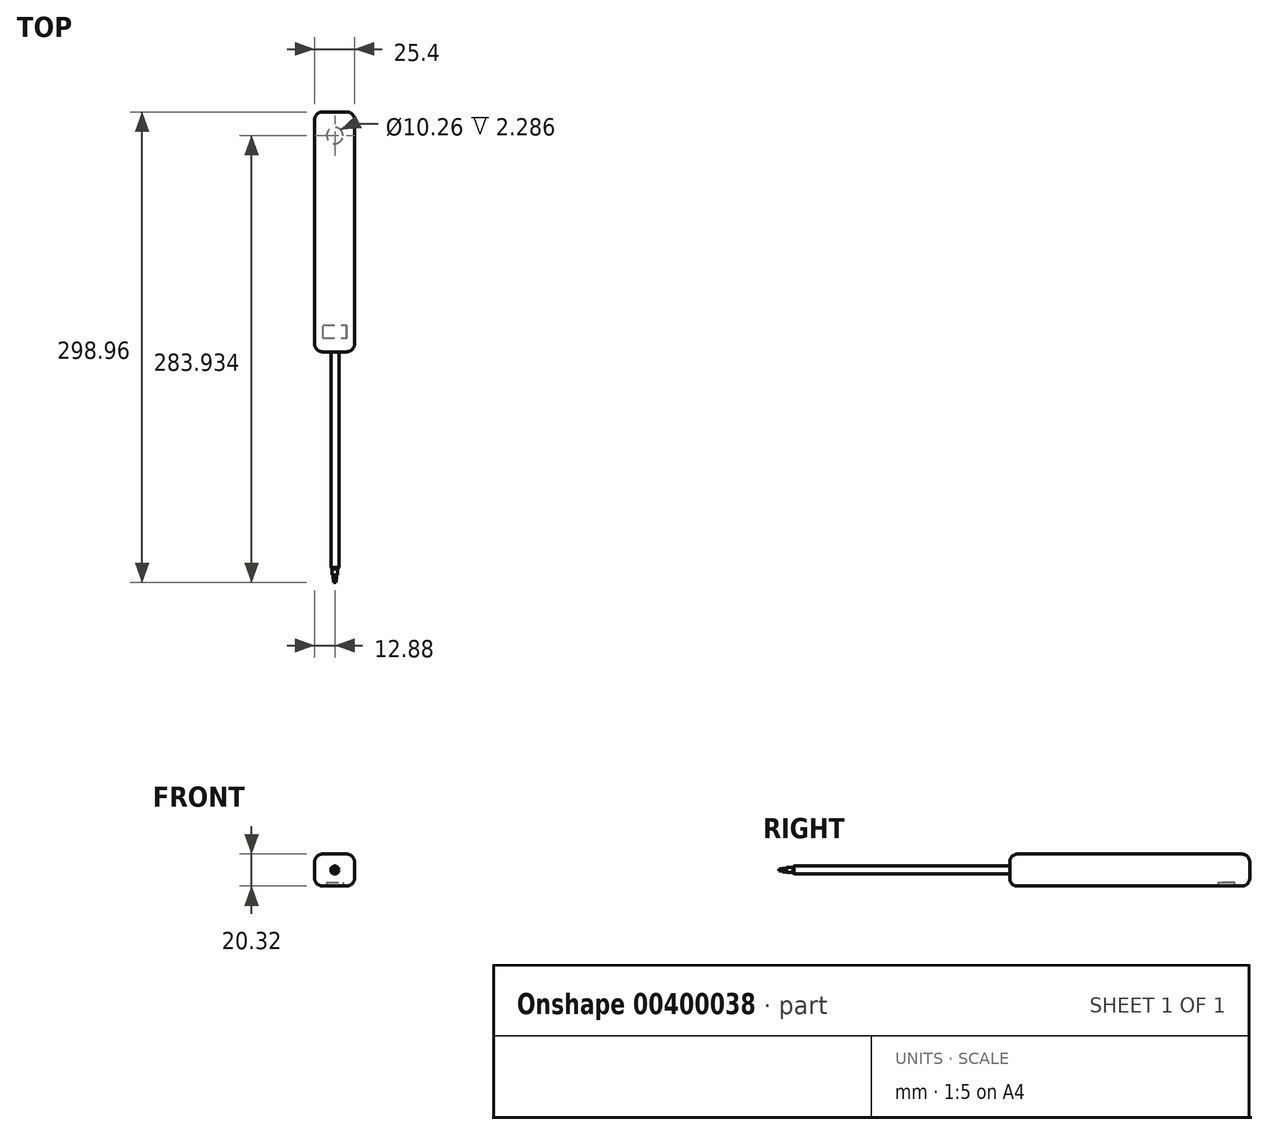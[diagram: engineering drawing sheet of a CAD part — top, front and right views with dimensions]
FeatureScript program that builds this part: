
annotation { "Feature Type Name" : "Feature", "Feature Type Description" : "" }
export const myFeature = defineFeature(function(context is Context, id is Id, definition is map)
    precondition{}
    {
        {
            var Q0;
            Q0=qCreatedBy(makeId("Front.planeOp"),FACE);
            var sketch = newSketch(context, id + "F0", { "sketchPlane" : qUnion([Q0])});
            skLineSegment(sketch, "E0.bottom", {"start": v(12.52, 10.1) * mm, "end": v(-12.88, 10.1) * mm});
            skLineSegment(sketch, "E0.top", {"start": v(12.52, -10.23) * mm, "end": v(-12.88, -10.23) * mm});
            skLineSegment(sketch, "E0.left", {"start": v(12.52, 10.1) * mm, "end": v(12.52, -10.23) * mm});
            skLineSegment(sketch, "E0.right", {"start": v(-12.88, 10.1) * mm, "end": v(-12.88, -10.23) * mm});
            skSolve(sketch);
        }
        {
            var Q0;
            Q0=makeQuery(id+"F0.imprint","IMPRINT",FACE,{"disambiguationData":[TD([[makeQuery(id+"F0.imprint","IMPRINT",EDGE,{"derivedFrom":sQuery(id+"F0.wireOp",EDGE,"E0.bottom")}),1.0]])]});
            extrude(context, id + "F1", {"entities" : qUnion([Q0]), "depth" : 127 * mm});
        }
        {
            var Q0;
            Q0=makeQuery(id+"F1.opExtrude","SWEPT_EDGE",EDGE,{"disambiguationData":[OSD([sQuery(id+"F0.wireOp",EDGE,"E0.bottom"),sQuery(id+"F0.wireOp",EDGE,"E0.left")])]});
            var Q1;
            Q1=makeQuery(id+"F1.opExtrude","SWEPT_EDGE",EDGE,{"disambiguationData":[OSD([sQuery(id+"F0.wireOp",EDGE,"E0.top"),sQuery(id+"F0.wireOp",EDGE,"E0.left")])]});
            fillet(context, id + "F2", {"entities" : qUnion([Q0, Q1]), "radius" : 5.08 * mm, "tangentPropagation" : true, "allowEdgeOverflow" : false});
        }
        {
            var Q0;
            Q0=makeQuery(id+"F1.opExtrude","SWEPT_EDGE",EDGE,{"disambiguationData":[OSD([sQuery(id+"F0.wireOp",EDGE,"E0.top"),sQuery(id+"F0.wireOp",EDGE,"E0.right")])]});
            fillet(context, id + "F3", {"entities" : qUnion([Q0]), "radius" : 5.08 * mm, "tangentPropagation" : true, "allowEdgeOverflow" : false});
        }
        {
            var Q0;
            Q0=makeQuery(id+"F1.opExtrude","SWEPT_EDGE",EDGE,{"disambiguationData":[OSD([sQuery(id+"F0.wireOp",EDGE,"E0.bottom"),sQuery(id+"F0.wireOp",EDGE,"E0.right")])]});
            var Q1;
            Q1=makeQuery(id+"F1.opExtrude","CAP_EDGE",EDGE,{"disambiguationData":[OSD([sQuery(id+"F0.wireOp",EDGE,"E0.right")])],"isStart":true});
            fillet(context, id + "F4", {"entities" : qUnion([Q0, Q1]), "radius" : 5.08 * mm, "tangentPropagation" : true, "allowEdgeOverflow" : false});
        }
        {
            var Q0;
            Q0=makeQuery(id+"F1.opExtrude","CAP_FACE",FACE,{"disambiguationData":[OSD([sQuery(id+"F0.wireOp",EDGE,"E0.bottom"),sQuery(id+"F0.wireOp",EDGE,"E0.top"),sQuery(id+"F0.wireOp",EDGE,"E0.left"),sQuery(id+"F0.wireOp",EDGE,"E0.right")])],"isStart":false});
            extrude(context, id + "F5", {"entities" : qUnion([Q0]), "operationType" : NewBodyOperationType.ADD, "depth" : 25.4 * mm});
        }
        {
            var Q0;
            Q0=makeQuery(id+"F5.opExtrude","CAP_FACE",FACE,{"disambiguationData":[OSD([sQuery(id+"F0.wireOp",EDGE,"E0.bottom"),sQuery(id+"F0.wireOp",EDGE,"E0.top"),sQuery(id+"F0.wireOp",EDGE,"E0.left"),sQuery(id+"F0.wireOp",EDGE,"E0.right")])],"isStart":false});
            var sketch = newSketch(context, id + "F6", { "sketchPlane" : qUnion([Q0])});
            skCircle(sketch, "E1", {"center": v(0, 0) * mm, "radius": 2.54 * mm});
            skSolve(sketch);
        }
        {
            var Q0;
            Q0=makeQuery(id+"F6.imprint","IMPRINT",FACE,{"disambiguationData":[TD([[makeQuery(id+"F6.imprint","IMPRINT",EDGE,{"derivedFrom":sQuery(id+"F6.wireOp",EDGE,"E1")}),1.0]])]});
            extrude(context, id + "F7", {"entities" : qUnion([Q0]), "operationType" : NewBodyOperationType.ADD, "depth" : 139.2 * mm});
        }
        {
            var Q0;
            {var subQ0=sQuery(id+"F0.wireOp",EDGE,"E0.right");var subQ1=sQuery(id+"F0.wireOp",EDGE,"E0.left");var subQ2=sQuery(id+"F0.wireOp",EDGE,"E0.top");var subQ3=sQuery(id+"F0.wireOp",EDGE,"E0.bottom");Q0=makeQuery(id+"F5.opExtrude","CAP_EDGE",EDGE,{"disambiguationData":[OSD([subQ3,subQ2,subQ1,subQ0]),TDD([makeQuery(id+"F2.opFillet","BLEND_EDGE",EDGE,{"blendedFrom":[makeQuery(id+"F1.opExtrude","SWEPT_EDGE",EDGE,{"disambiguationData":[OSD([subQ3,subQ1])]}),makeQuery(id+"F1.opExtrude","CAP_FACE",FACE,{"disambiguationData":[OSD([subQ3,subQ2,subQ1,subQ0])],"isStart":false})],"blendedInto":[makeQuery(id+"F1.opExtrude","CAP_FACE",FACE,{"disambiguationData":[OSD([subQ3,subQ2,subQ1,subQ0])],"isStart":false})]})])],"isStart":false});}
            fillet(context, id + "F8", {"entities" : qUnion([Q0]), "radius" : 5.08 * mm, "tangentPropagation" : true, "allowEdgeOverflow" : false});
        }
        {
            var Q0;
            Q0=makeQuery(id+"F7.opExtrude","CAP_FACE",FACE,{"disambiguationData":[OSD([sQuery(id+"F6.wireOp",EDGE,"E1")])],"isStart":false});
            var sketch = newSketch(context, id + "F9", { "sketchPlane" : qUnion([Q0])});
            skPoint(sketch, "E2.center.orphan", {"position": v(0, 0) * mm});
            skCircle(sketch, "E3", {"center": v(0, 0) * mm, "radius": 1.61 * mm});
            skSolve(sketch);
        }
        {
            var Q0;
            Q0 = qSketchRegion(id + "F9", true);
            extrude(context, id + "F10", {"entities" : qUnion([Q0]), "operationType" : NewBodyOperationType.ADD, "depth" : 2.54 * mm});
        }
        {
            var Q0;
            Q0=makeQuery(id+"F10.opExtrude","CAP_FACE",FACE,{"disambiguationData":[OSD([sQuery(id+"F9.wireOp",EDGE,"E3")])],"isStart":false});
            var sketch = newSketch(context, id + "F11", { "sketchPlane" : qUnion([Q0])});
            skCircle(sketch, "E4", {"center": v(0, 0) * mm, "radius": 1.08 * mm});
            skSolve(sketch);
        }
        {
            var Q0;
            Q0=makeQuery(id+"F11.imprint","IMPRINT",FACE,{"disambiguationData":[TD([[makeQuery(id+"F11.imprint","IMPRINT",EDGE,{"derivedFrom":sQuery(id+"F11.wireOp",EDGE,"E4")}),1.0]])]});
            extrude(context, id + "F12", {"entities" : qUnion([Q0]), "operationType" : NewBodyOperationType.ADD, "depth" : 2.54 * mm});
        }
        {
            var Q0;
            Q0=makeQuery(id+"F12.opExtrude","CAP_FACE",FACE,{"disambiguationData":[OSD([sQuery(id+"F11.wireOp",EDGE,"E4")])],"isStart":false});
            var sketch = newSketch(context, id + "F13", { "sketchPlane" : qUnion([Q0])});
            skCircle(sketch, "E5", {"center": v(0, 0) * mm, "radius": 0.68 * mm});
            skSolve(sketch);
        }
        {
            var Q0;
            Q0=makeQuery(id+"F13.imprint","IMPRINT",FACE,{"disambiguationData":[TD([[makeQuery(id+"F13.imprint","IMPRINT",EDGE,{"derivedFrom":sQuery(id+"F13.wireOp",EDGE,"E5")}),1.0]])]});
            extrude(context, id + "F14", {"entities" : qUnion([Q0]), "operationType" : NewBodyOperationType.ADD, "depth" : 2.3 * mm});
        }
        {
            var Q0;
            Q0=makeQuery(id+"F7.opExtrude","CAP_EDGE",EDGE,{"disambiguationData":[OSD([sQuery(id+"F6.wireOp",EDGE,"E1")])],"isStart":false});
            chamfer(context, id + "F15", {"entities" : qUnion([Q0]), "width" : 2.3 * mm, "tangentPropagation" : true});
        }
        {
            var Q0;
            {var subQ0=sQuery(id+"F0.wireOp",EDGE,"E0.top");Q0=makeQuery(id+"F5.boolean.opBoolean","MERGE",FACE,{"derivedFrom":[makeQuery(id+"F1.opExtrude","SWEPT_FACE",FACE,{"disambiguationData":[OSD([subQ0])]}),makeQuery(id+"F5.opExtrude","SWEPT_FACE",FACE,{"disambiguationData":[OSD([subQ0])]})]});}
            var sketch = newSketch(context, id + "F16", { "sketchPlane" : qUnion([Q0])});
            skCircle(sketch, "E6", {"center": v(0, 15.03) * mm, "radius": 5.13 * mm});
            skSolve(sketch);
        }
        {
            var Q0;
            Q0=makeQuery(id+"F16.imprint","IMPRINT",FACE,{"disambiguationData":[TD([[makeQuery(id+"F16.imprint","IMPRINT",EDGE,{"derivedFrom":sQuery(id+"F16.wireOp",EDGE,"E6")}),1.0]])]});
            var Q1;
            Q1=sQuery(id+"F16.wireOp",EDGE,"E6");
            extrude(context, id + "F17", {"entities" : qUnion([Q0]), "operationType" : NewBodyOperationType.REMOVE, "surfaceEntities" : qUnion([Q1]), "oppositeDirection" : true, "depth" : 2.3 * mm});
        }
        {
            var Q0;
            Q0=makeQuery(id+"F16.imprint","IMPRINT",FACE,{"disambiguationData":[TD([[makeQuery(id+"F16.imprint","IMPRINT",EDGE,{"derivedFrom":sQuery(id+"F16.wireOp",EDGE,"E6")}),-1.0]])]});
            var sketch = newSketch(context, id + "F18", { "sketchPlane" : qUnion([Q0])});
            skLineSegment(sketch, "E7.bottom", {"start": v(-7.53, 143.55) * mm, "end": v(7.62, 143.55) * mm});
            skLineSegment(sketch, "E7.top", {"start": v(-7.53, 135.28) * mm, "end": v(7.62, 135.28) * mm});
            skLineSegment(sketch, "E7.left", {"start": v(-7.53, 143.55) * mm, "end": v(-7.53, 135.28) * mm});
            skLineSegment(sketch, "E7.right", {"start": v(7.62, 143.55) * mm, "end": v(7.62, 135.28) * mm});
            skSolve(sketch);
        }
        {
            var Q0;
            Q0 = qSketchRegion(id + "F18", true);
            extrude(context, id + "F19", {"entities" : qUnion([Q0]), "operationType" : NewBodyOperationType.ADD, "depth" : 0 * mm});
        }
    });
